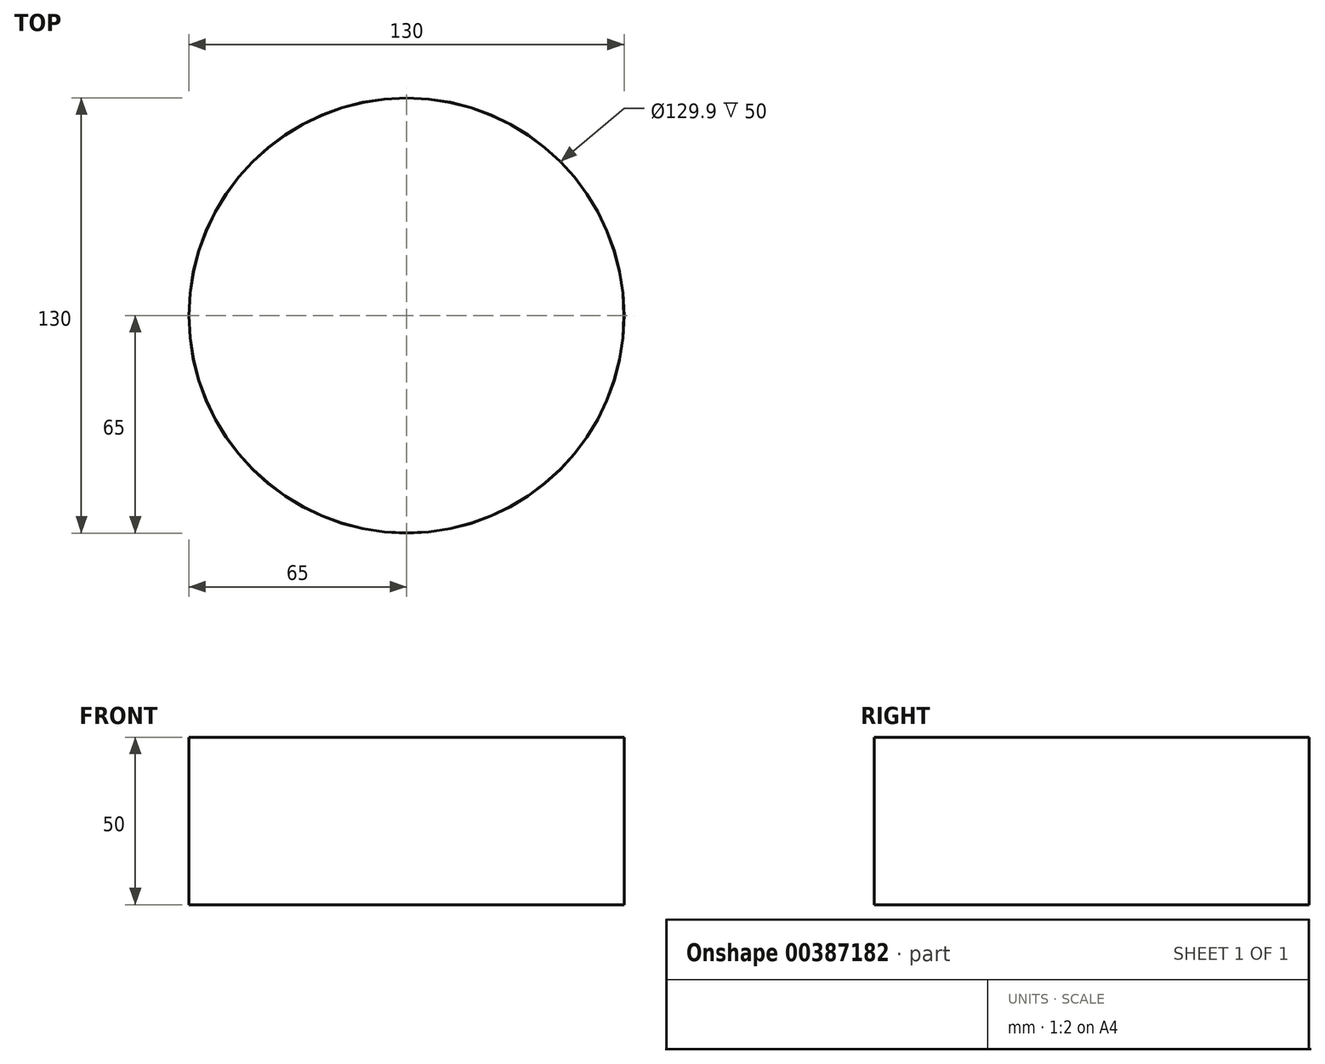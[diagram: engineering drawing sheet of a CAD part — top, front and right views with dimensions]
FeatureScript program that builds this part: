
annotation { "Feature Type Name" : "Feature", "Feature Type Description" : "" }
export const myFeature = defineFeature(function(context is Context, id is Id, definition is map)
    precondition{}
    {
        {
            var Q0;
            Q0=qCreatedBy(makeId("Top.planeOp"),FACE);
            var sketch = newSketch(context, id + "F0", { "sketchPlane" : qUnion([Q0])});
            skCircle(sketch, "E0", {"center": v(0, 0) * mm, "radius": 65 * mm});
            skCircle(sketch, "E1", {"center": v(0, 0) * mm, "radius": 64.95 * mm});
            skSolve(sketch);
        }
        {
            var Q0;
            Q0=makeQuery(id+"F0.imprint","IMPRINT",FACE,{"disambiguationData":[TD([[makeQuery(id+"F0.imprint","IMPRINT",EDGE,{"derivedFrom":sQuery(id+"F0.wireOp",EDGE,"E0")}),1.0]])]});
            extrude(context, id + "F1", {"entities" : qUnion([Q0]), "depth" : 50 * mm, "offsetDistance" : 25 * mm});
        }
    });
